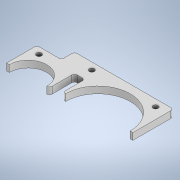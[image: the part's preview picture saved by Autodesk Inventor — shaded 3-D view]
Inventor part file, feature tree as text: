
AUTODESK INVENTOR PART (.ipt)
format: ipt  version: 2021 (Build 250183000, 183)  size: 260,608 bytes
history: native  units: mm
features: sketch x6, extrude x5, projected_geometry x2, hole x1, fillet x1
ambient origin geometry x8: Origin, YZ Plane, XZ Plane, XY Plane, X Axis, Y Axis, Z Axis, Center Point
bodies: Solid1 (feature_tree)
feature tree (15):
  extrude  "Extrusion1"  Depth=116.5mm
  extrude  "Extrusion2"  Depth=5.0mm
  extrude  "Extrusion3"  Depth=27.7mm
  hole  "Hole1"  [1 undecoded]
  extrude  "Extrusion4"  Depth=112.5mm
  extrude  "Extrusion6"  Depth=2.0mm
  fillet  "Fillet3"  Radius=30.9mm
  sketch  "Sketch1"  dims[d0=112.5mm d1=116.5mm]
  sketch  "Sketch2"  dims[d2=5.0mm d3=0.0mm d4=47.7mm]
  sketch  "Sketch4"  dims[d5=27.7mm d6=27.7mm]
  sketch  "Sketch5"  dims[d7=27.7mm d8=27.7mm]
  projected_geometry  "Projected Loop1"
  projected_geometry  "Projected Loop2"
  sketch  "Sketch6"  dims[d9=116.5mm d10=112.5mm]
  sketch  "Sketch8"  dims[d13=37.0mm d14=18.5mm d15=30.9mm d16=5.0mm d17=0.0mm d18=18.0mm d19=35.0mm d20=35.0mm d36=10.0mm d37=0.0mm d40=5.5mm d41=5.5mm d44=15.0mm d46=3.8mm d47=6.0mm d48=4.0mm d49=2.0mm d50=90.0deg d51=8.0mm d52=20.594885mm d54=2.0mm d55=2.0mm d56=2.0mm d57=2.0mm d58=2.0mm d59=2.0mm d60=2.0mm d61=2.0mm d62=2.0mm d63=27.7mm d64=10.0mm d65=10.0mm d66=25.8mm d67=23.25mm d68=23.25mm d69=37.0mm d70=27.7mm d71=27.7mm d72=19.15mm d73=50.85mm d74=46.75mm d75=2.0mm d76=6.182153mm d77=31.7mm d78=51.7mm d79=30.9mm d80=3.4mm d81=11.9mm d82=61.0mm d83=47.7mm d84=28.0mm d85=18.5mm d86=30.27mm d87=27.7mm d88=2.0mm d89=30.27mm d90=2.0mm d91=112.5mm d92=116.5mm d93=25.8mm d94=28.0mm d96=14.0mm d97=2.0mm d99=6.5mm d100=36.0mm d101=8.0mm d102=18.0mm d103=10.0mm d104=10.0mm d105=0.0mm d109=0.3mm d110=0.0mm d111=2.0mm]
note: 1 required parameter value undecoded (feature->parameter linkage not recoverable at this tier; creation-order binding heuristic only, values carry confidence <= 0.55)
